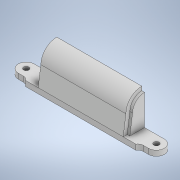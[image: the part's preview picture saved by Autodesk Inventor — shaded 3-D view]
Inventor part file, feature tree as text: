
AUTODESK INVENTOR PART (.ipt)
format: ipt  version: 2022 (Build 260153000, 153)  size: 211,456 bytes
history: native  units: mm
features: extrude x4, sketch x4, mirror x1
ambient origin geometry x8: Origin, YZ Plane, XZ Plane, XY Plane, X Axis, Y Axis, Z Axis, Center Point
bodies: Solid1 (feature_tree)
feature tree (9):
  extrude  "Extrusion1"  Depth=6.0mm
  extrude  "Extrusion2"  Depth=2.0mm
  extrude  "Extrusion3"  Depth=3.0mm
  extrude  "Extrusion4"  Depth=3.0mm
  mirror  "Mirror1"
  sketch  "Sketch1"  dims[d0=24.5mm d1=6.0mm]
  sketch  "Sketch2"  dims[d2=2.0mm d3=2.0mm]
  sketch  "Sketch3"  dims[d4=3.0mm d5=3.0mm]
  sketch  "Sketch4"  dims[d6=9.0mm d7=3.0mm d8=18.0mm d9=4.0mm d10=4.0mm d11=2.0mm d12=2.0mm d13=0.0mm d14=10.0mm d15=0.0mm d16=7.0mm d17=3.0mm d18=16.0mm d19=0.0mm d20=6.0mm d21=3.0mm d22=7.0mm d23=4.0mm d24=9.0mm d25=1.5mm d26=1.0mm d27=1.0mm d28=0.0mm d29=0.0mm d30=0.0mm d31=0.0mm]
